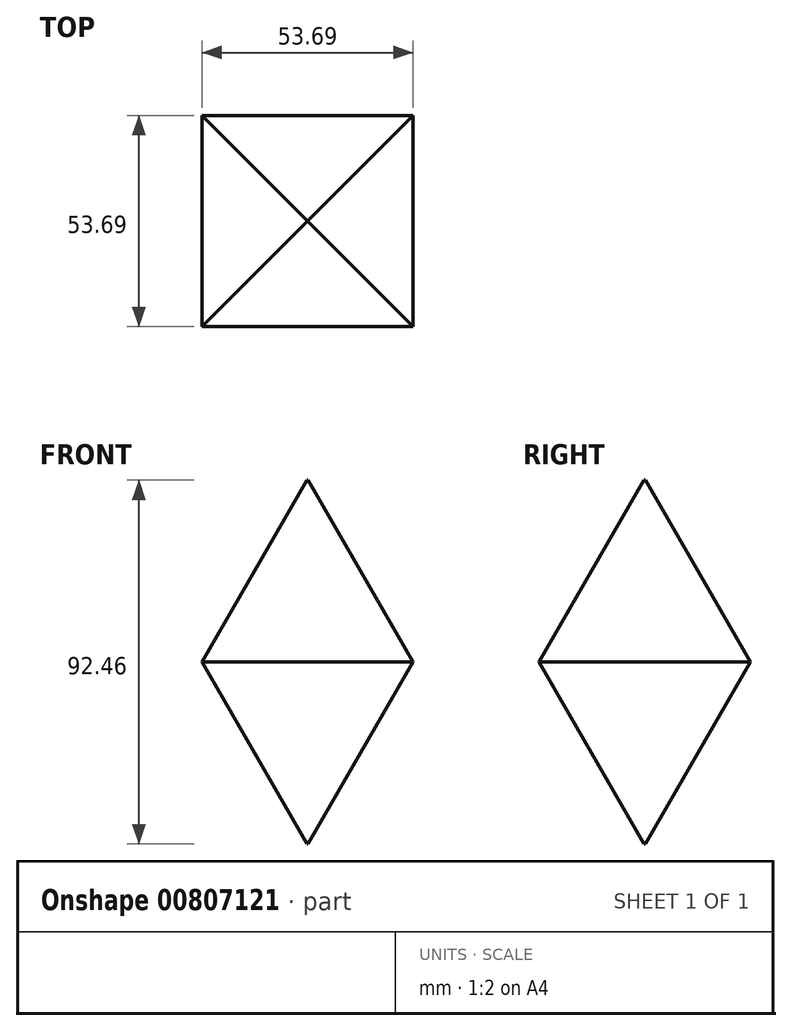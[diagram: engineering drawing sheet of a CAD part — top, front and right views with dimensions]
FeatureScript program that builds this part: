
annotation { "Feature Type Name" : "Feature", "Feature Type Description" : "" }
export const myFeature = defineFeature(function(context is Context, id is Id, definition is map)
    precondition{}
    {
        {
            var Q0;
            Q0=qCreatedBy(makeId("Top.planeOp"),FACE);
            var sketch = newSketch(context, id + "F0", { "sketchPlane" : qUnion([Q0])});
            skLineSegment(sketch, "E0.bottom", {"start": v(11.87, -14.38) * mm, "end": v(-41.82, -14.38) * mm});
            skLineSegment(sketch, "E0.top", {"start": v(11.87, 39.3) * mm, "end": v(-41.82, 39.3) * mm});
            skLineSegment(sketch, "E0.left", {"start": v(11.87, -14.38) * mm, "end": v(11.87, 39.3) * mm});
            skLineSegment(sketch, "E0.right", {"start": v(-41.82, -14.38) * mm, "end": v(-41.82, 39.3) * mm});
            skPoint(sketch, "E0.middle", {"position": v(-14.97, 12.46) * mm});
            skSolve(sketch);
        }
        {
            var Q0;
            Q0 = qSketchRegion(id + "F0", true);
            extrude(context, id + "F1", {"entities" : qUnion([Q0]), "depth" : 46.23 * mm, "offsetDistance" : 25.4 * mm, "hasDraft" : true, "draftAngle" : 30 * degree, "draftPullDirection" : true, "hasSecondDirection" : true, "secondDirectionOppositeDirection" : true, "secondDirectionDepth" : 46.23 * mm, "hasSecondDirectionDraft" : true, "secondDirectionDraftAngle" : 30 * degree, "secondDirectionDraftPullDirection" : true});
        }
    });
